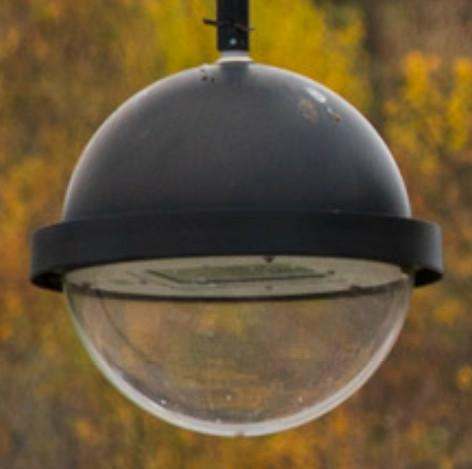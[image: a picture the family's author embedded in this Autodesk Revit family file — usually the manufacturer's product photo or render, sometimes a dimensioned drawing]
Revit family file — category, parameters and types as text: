
# Revit family: GALAD ДСУ24 LED !
name_source: partatom
category: Осветительные приборы
revit_build: Autodesk Revit 2018 (Build: 20180423_1000(x64)
units: mm (PartAtom-declared; Revit-internal decimal feet)

## family parameters
Источник света = Да
Общий = Нет
Основа = Грань
При загрузке вырезать с полостями = Нет
Размер круглого соединителя = Использовать диаметр
Тип детали = Нормальный
Точка расчета площади = Нет

## types (2) — shared parameters
ADSK_Версия Revit = 2018
ADSK_Версия семейства = 1.01
ADSK_Единица измерения = шт.
ADSK_Завод-изготовитель = Лихославльский завод Светотехника
ADSK_Классификация нагрузок = Освещение
ADSK_Количество = 1
ADSK_Количество фаз = 1
ADSK_Коэффициент мощности = 0.95
ADSK_Масса = 12
ADSK_Материал = Термостойкая ударопрочная пластмасса
ADSK_Напряжение = 230 В
ADSK_Размер_Высота = 565 мм
ADSK_Размер_Длина = 530 мм
ADSK_Размер_Ширина = 530 мм
ADSK_Ток = 0 А
IP = IP54
URL = https://galad.ru
Блок аварийного питания = Нет
Видимая форма излучения при визуализации = Нет
Группа модели = Светильники
Диапазон цветовой температуры = 3985±275
Изготовитель = Лихославльский завод Светотехника
Излучение по длине прямоугольника = 250 мм
Излучение по ширине прямоугольника = 250 мм
Класс Защиты = 1
Класс защиты от поражения электрическим током = 1
Класс светораспределения = П
Климатическая зона = У1
Климатическое исполнение = -45…+40 °С
Коэффициент пульсации = 5
Область использования = Освещение улиц и дорог с высокой, средней и слабой интенсивностью движения транспорта, а также площадей, функционально-декоративного освещения парков, бульваров, коттеджных поселков, железнодорожных платформ и станций, мостов, территорий дворов, школ.
Описание = Светильники серии ДСУ24 "Сатурн"  предназначены для наружного освещения: освещение улиц и дорог с высокой, средней и слабой интенсивностью движения транспорта, а также площадей, функционально-декоративного освещения парков, бульваров, коттеджных поселков, железнодорожных платформ и станций, мостов, территорий дворов, школ.
Светофильтр = 16777215
Смещение цветовой температуры при затухании лампы = <Нет>
Снижение светового потока во время разгорания = не более 10%
Срок службы = 12 лет
Тип КСС = широкая боковая
Тип ПРА = электронный драйвер
Тип источника света = LED
Тип монтажной поверхности = Подвесной
Тип продукции = Светильник
Тип устройства управления светодиодами = без управления
Угол наклона = 90.00°
Цветопередача = 70
Частота = 50
zero-valued in all types: Отметка по умолчанию

## per-type parameters (varying)
| type | ADSK_Код изделия | ADSK_Номинальная мощность | ADSK_Обозначение | ADSK_Полная мощность | ADSK_Энергоэффективность | Полная установленная мощность | Световая отдача | Файл фотометрической сетки |
| GALAD ДСУ24-75-001 У1 | 13066 | 75 Вт | ГОСТ 12.2.007.0-75, ГОСТ 17516.1, ГОСТ 15150-69, ГОСТ Р 54351 | 79 В·А | 108 лм/Вт | 79 В·А | 108 | galaddsu24-75-001-shb1.ies |
| GALAD ДСУ24-40-001 У1 | 13065 | 40 Вт | ГОСТ 12.2.007.0-75, ГОСТ 17516.1, ГОСТ 15150-69, ГОСТ Р 54350 | 42 В·А | 120 лм/Вт | 42 В·А | 120 | galaddsu24-40-001-shb1.ies |

note: column(s) folded — value = type name in every type: ADSK_Марка, ADSK_Наименование, ADSK_Наименование краткое
